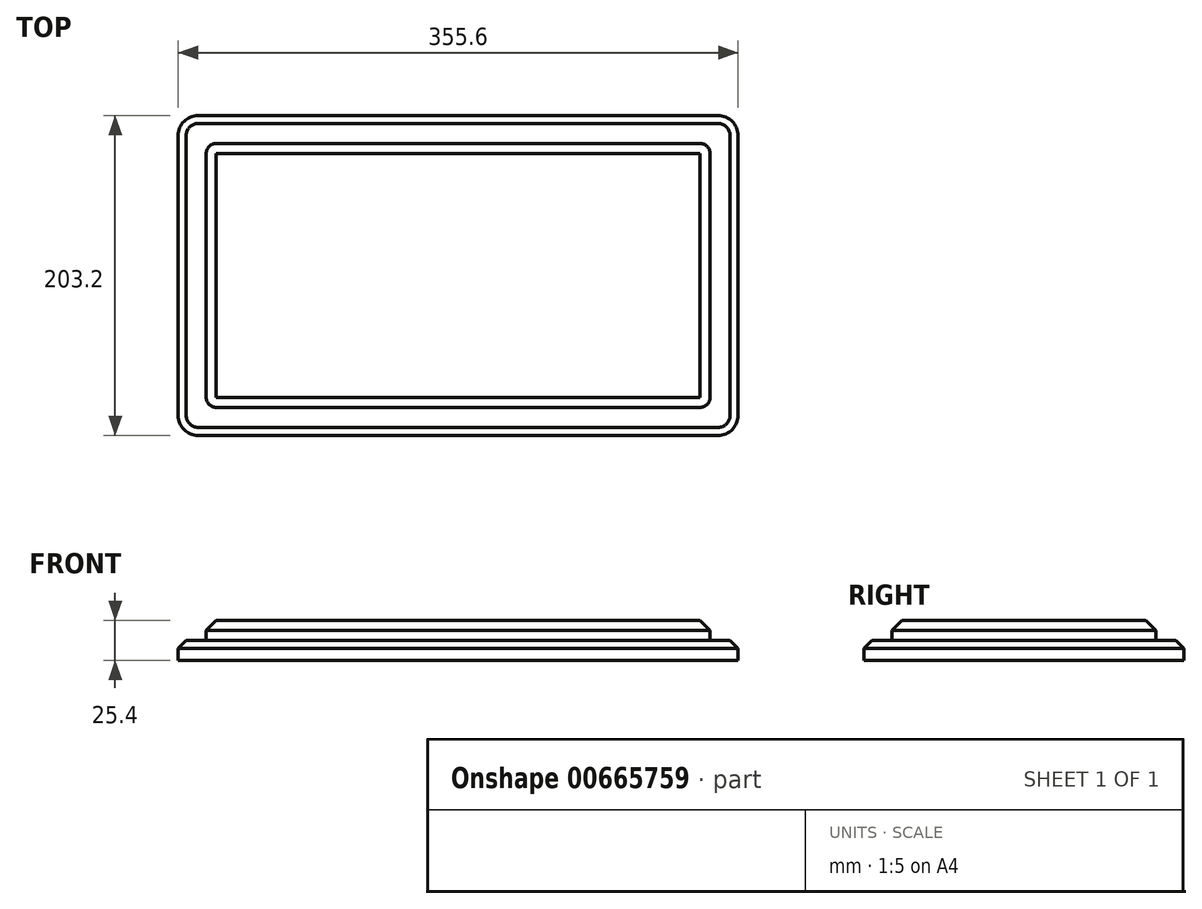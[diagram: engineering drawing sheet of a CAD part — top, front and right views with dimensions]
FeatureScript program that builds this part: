
annotation { "Feature Type Name" : "Feature", "Feature Type Description" : "" }
export const myFeature = defineFeature(function(context is Context, id is Id, definition is map)
    precondition{}
    {
        {
            var Q0;
            Q0=qCreatedBy(makeId("Top.planeOp"),FACE);
            var sketch = newSketch(context, id + "F0", { "sketchPlane" : qUnion([Q0])});
            skLineSegment(sketch, "E0", {"start": v(0, 12.7) * mm, "end": v(0, 190.5) * mm});
            skLineSegment(sketch, "E1", {"start": v(12.7, 203.2) * mm, "end": v(342.9, 203.2) * mm});
            skLineSegment(sketch, "E2", {"start": v(355.6, 190.5) * mm, "end": v(355.6, 12.7) * mm});
            skLineSegment(sketch, "E3", {"start": v(342.9, 0) * mm, "end": v(12.7, 0) * mm});
            skPoint(sketch, "E4.visualSharp", {"position": v(0, 203.2) * mm});
            skArc(sketch, "E4.filletArc", {"start": v(12.7, 203.2) * mm, "mid": v(3.72, 199.48) * mm, "end": v(0, 190.5) * mm});
            skPoint(sketch, "E5.visualSharp", {"position": v(0, 0) * mm});
            skArc(sketch, "E5.filletArc", {"start": v(0, 12.7) * mm, "mid": v(3.72, 3.72) * mm, "end": v(12.7, 0) * mm});
            skPoint(sketch, "E6.visualSharp", {"position": v(355.6, 0) * mm});
            skArc(sketch, "E6.filletArc", {"start": v(342.9, 0) * mm, "mid": v(351.88, 3.72) * mm, "end": v(355.6, 12.7) * mm});
            skPoint(sketch, "E7.visualSharp", {"position": v(355.6, 203.2) * mm});
            skArc(sketch, "E7.filletArc", {"start": v(355.6, 190.5) * mm, "mid": v(351.88, 199.48) * mm, "end": v(342.9, 203.2) * mm});
            skSolve(sketch);
        }
        {
            var Q0;
            Q0=makeQuery(id+"F0.imprint","IMPRINT",FACE,{"disambiguationData":[TD([[makeQuery(id+"F0.imprint","IMPRINT",EDGE,{"derivedFrom":sQuery(id+"F0.wireOp",EDGE,"E0")}),-1.0]])]});
            extrude(context, id + "F1", {"entities" : qUnion([Q0]), "depth" : 12.7 * mm, "offsetDistance" : 25.4 * mm});
        }
        {
            var Q0;
            Q0=makeQuery(id+"F1.opExtrude","CAP_EDGE",EDGE,{"disambiguationData":[OSD([sQuery(id+"F0.wireOp",EDGE,"E0")])],"isStart":false});
            chamfer(context, id + "F2", {"entities" : qUnion([Q0]), "width" : 5.08 * mm, "tangentPropagation" : true});
        }
        {
            var Q0;
            Q0=makeQuery(id+"F1.opExtrude","CAP_FACE",FACE,{"disambiguationData":[OSD([sQuery(id+"F0.wireOp",EDGE,"E0"),sQuery(id+"F0.wireOp",EDGE,"E1"),sQuery(id+"F0.wireOp",EDGE,"E2"),sQuery(id+"F0.wireOp",EDGE,"E3"),sQuery(id+"F0.wireOp",EDGE,"E4.filletArc"),sQuery(id+"F0.wireOp",EDGE,"E5.filletArc"),sQuery(id+"F0.wireOp",EDGE,"E6.filletArc"),sQuery(id+"F0.wireOp",EDGE,"E7.filletArc")])],"isStart":false});
            var sketch = newSketch(context, id + "F3", { "sketchPlane" : qUnion([Q0])});
            skLineSegment(sketch, "E8", {"start": v(5.08, 101.6) * mm, "end": v(17.78, 101.6) * mm, "construction": true});
            skLineSegment(sketch, "E9", {"start": v(177.8, 198.12) * mm, "end": v(177.8, 185.42) * mm, "construction": true});
            skLineSegment(sketch, "E10", {"start": v(17.78, 101.6) * mm, "end": v(17.78, 179.07) * mm});
            skLineSegment(sketch, "E11", {"start": v(24.13, 185.42) * mm, "end": v(177.8, 185.42) * mm});
            skLineSegment(sketch, "E12.MirrorCS", {"start": v(331.47, 185.42) * mm, "end": v(177.8, 185.42) * mm});
            skLineSegment(sketch, "E13.MirrorCS", {"start": v(337.82, 101.6) * mm, "end": v(337.82, 179.07) * mm});
            skLineSegment(sketch, "E14.MirrorCS", {"start": v(17.78, 101.6) * mm, "end": v(17.78, 24.13) * mm});
            skLineSegment(sketch, "E15.MirrorCS", {"start": v(24.13, 17.78) * mm, "end": v(177.8, 17.78) * mm});
            skLineSegment(sketch, "E16.MirrorCS", {"start": v(331.47, 17.78) * mm, "end": v(177.8, 17.78) * mm});
            skLineSegment(sketch, "E17.MirrorCS", {"start": v(337.82, 101.6) * mm, "end": v(337.82, 24.13) * mm});
            skPoint(sketch, "E18.visualSharp", {"position": v(17.78, 185.42) * mm});
            skArc(sketch, "E18.filletArc", {"start": v(24.13, 185.42) * mm, "mid": v(19.64, 183.56) * mm, "end": v(17.78, 179.07) * mm});
            skPoint(sketch, "E19.visualSharp", {"position": v(17.78, 17.78) * mm});
            skArc(sketch, "E19.filletArc", {"start": v(17.78, 24.13) * mm, "mid": v(19.64, 19.64) * mm, "end": v(24.13, 17.78) * mm});
            skPoint(sketch, "E20.visualSharp", {"position": v(337.82, 17.78) * mm});
            skArc(sketch, "E20.filletArc", {"start": v(331.47, 17.78) * mm, "mid": v(335.96, 19.64) * mm, "end": v(337.82, 24.13) * mm});
            skPoint(sketch, "E21.visualSharp", {"position": v(337.82, 185.42) * mm});
            skArc(sketch, "E21.filletArc", {"start": v(337.82, 179.07) * mm, "mid": v(335.96, 183.56) * mm, "end": v(331.47, 185.42) * mm});
            skSolve(sketch);
        }
        {
            var Q0;
            Q0=makeQuery(id+"F3.imprint","IMPRINT",FACE,{"disambiguationData":[TD([[makeQuery(id+"F3.imprint","IMPRINT",EDGE,{"derivedFrom":sQuery(id+"F3.wireOp",EDGE,"E10")}),-1.0]])]});
            extrude(context, id + "F4", {"entities" : qUnion([Q0]), "operationType" : NewBodyOperationType.ADD, "depth" : 12.7 * mm, "offsetDistance" : 25.4 * mm});
        }
        {
            var Q0;
            Q0=makeQuery(id+"F4.opExtrude","CAP_EDGE",EDGE,{"disambiguationData":[OSD([sQuery(id+"F3.wireOp",EDGE,"E15.MirrorCS"),sQuery(id+"F3.wireOp",EDGE,"E16.MirrorCS")])],"isStart":false});
            chamfer(context, id + "F5", {"entities" : qUnion([Q0]), "width" : 6.35 * mm, "tangentPropagation" : true});
        }
    });
